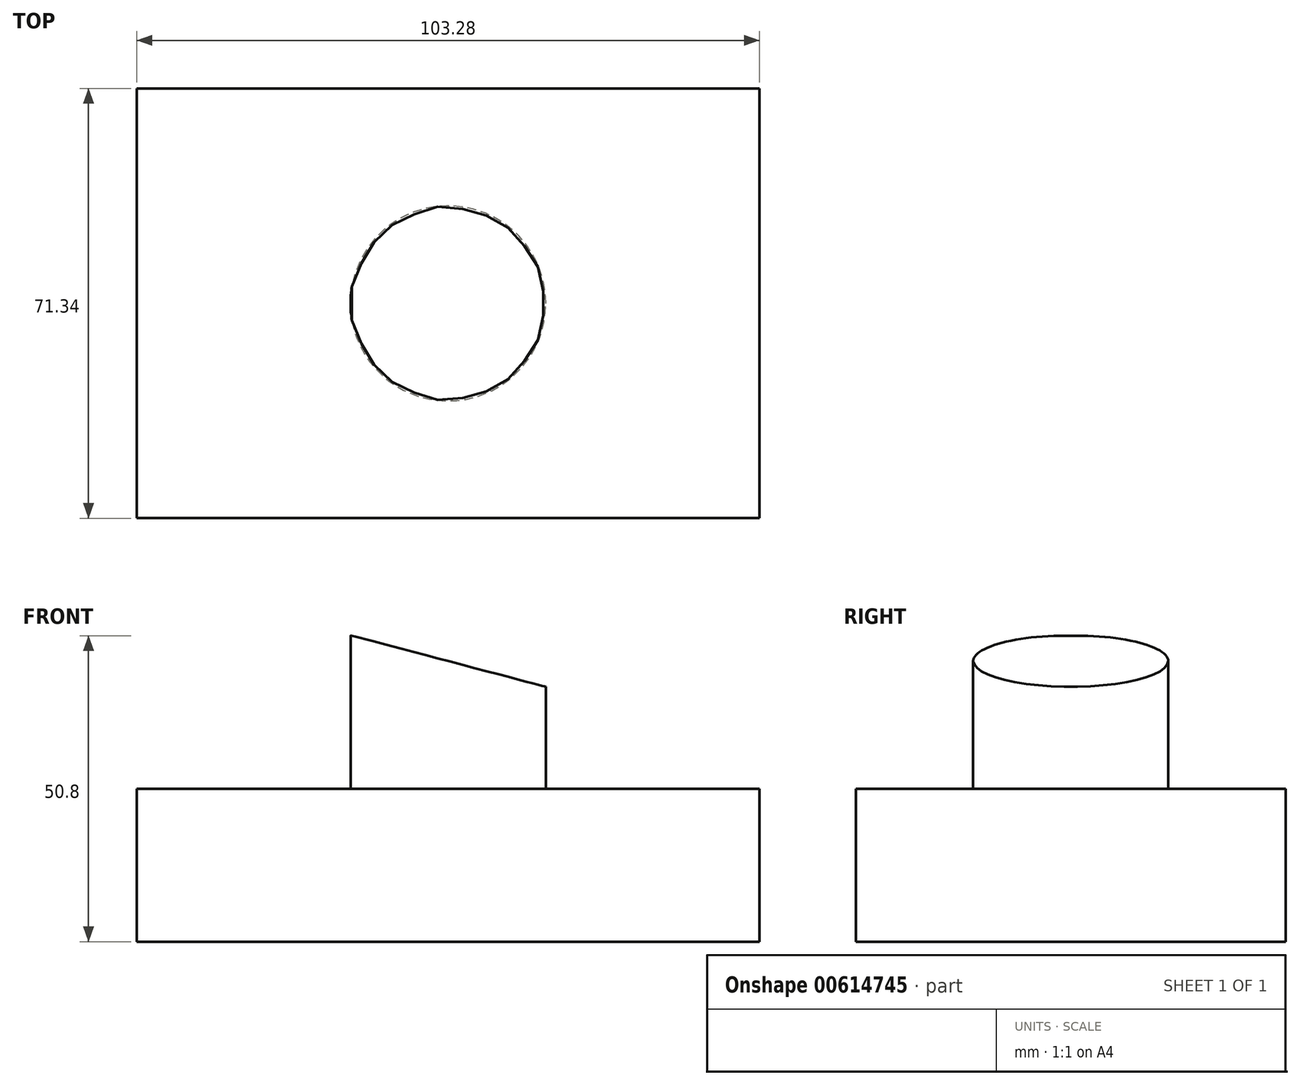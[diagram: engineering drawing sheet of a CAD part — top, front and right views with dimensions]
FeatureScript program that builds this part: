
annotation { "Feature Type Name" : "Feature", "Feature Type Description" : "" }
export const myFeature = defineFeature(function(context is Context, id is Id, definition is map)
    precondition{}
    {
        {
            var Q0;
            Q0=qCreatedBy(makeId("Top.planeOp"),FACE);
            var sketch = newSketch(context, id + "F0", { "sketchPlane" : qUnion([Q0])});
            skLineSegment(sketch, "E0.bottom", {"start": v(51.64, 35.67) * mm, "end": v(-51.64, 35.67) * mm});
            skLineSegment(sketch, "E0.top", {"start": v(51.64, -35.67) * mm, "end": v(-51.64, -35.67) * mm});
            skLineSegment(sketch, "E0.left", {"start": v(51.64, 35.67) * mm, "end": v(51.64, -35.67) * mm});
            skLineSegment(sketch, "E0.right", {"start": v(-51.64, 35.67) * mm, "end": v(-51.64, -35.67) * mm});
            skPoint(sketch, "E0.middle", {"position": v(0, 0) * mm});
            skSolve(sketch);
        }
        {
            var Q0;
            Q0=makeQuery(id+"F0.imprint","IMPRINT",FACE,{"disambiguationData":[TD([[makeQuery(id+"F0.imprint","IMPRINT",EDGE,{"derivedFrom":sQuery(id+"F0.wireOp",EDGE,"E0.bottom")}),1.0]])]});
            extrude(context, id + "F1", {"entities" : qUnion([Q0]), "depth" : 25.4 * mm, "offsetDistance" : 25.4 * mm});
        }
        {
            var Q0;
            Q0=makeQuery(id+"F1.opExtrude","CAP_FACE",FACE,{"disambiguationData":[OSD([sQuery(id+"F0.wireOp",EDGE,"E0.bottom"),sQuery(id+"F0.wireOp",EDGE,"E0.top"),sQuery(id+"F0.wireOp",EDGE,"E0.left"),sQuery(id+"F0.wireOp",EDGE,"E0.right")])],"isStart":false});
            var sketch = newSketch(context, id + "F2", { "sketchPlane" : qUnion([Q0])});
            skCircle(sketch, "E1", {"center": v(0, 0) * mm, "radius": 16.2 * mm});
            skSolve(sketch);
        }
        {
            var Q0;
            Q0=makeQuery(id+"F2.imprint","IMPRINT",FACE,{"disambiguationData":[TD([[makeQuery(id+"F2.imprint","IMPRINT",EDGE,{"derivedFrom":sQuery(id+"F2.wireOp",EDGE,"E1")}),1.0]])]});
            extrude(context, id + "F3", {"entities" : qUnion([Q0]), "operationType" : NewBodyOperationType.ADD, "depth" : 25.4 * mm, "offsetDistance" : 25.4 * mm});
        }
        {
            var Q0;
            Q0=qCreatedBy(makeId("Front.planeOp"),FACE);
            var sketch = newSketch(context, id + "F4", { "sketchPlane" : qUnion([Q0])});
            skLineSegment(sketch, "E2", {"start": v(-16.2, 50.87) * mm, "end": v(16.52, 50.87) * mm});
            skLineSegment(sketch, "E3", {"start": v(16.52, 50.87) * mm, "end": v(16.52, 42.23) * mm});
            skLineSegment(sketch, "E4", {"start": v(16.52, 42.23) * mm, "end": v(-16.2, 50.87) * mm});
            skSolve(sketch);
        }
        {
            var Q0;
            Q0 = qSketchRegion(id + "F4", true);
            extrude(context, id + "F5", {"entities" : qUnion([Q0]), "operationType" : NewBodyOperationType.REMOVE, "oppositeDirection" : true, "depth" : 25.4 * mm, "offsetDistance" : 25.4 * mm});
        }
        {
            var Q0;
            Q0=makeQuery(id+"F5.boolean.opBoolean","COPY",FACE,{"derivedFrom":makeQuery(id+"F5.opExtrude","CAP_FACE",FACE,{"disambiguationData":[OSD([sQuery(id+"F4.wireOp",EDGE,"E2"),sQuery(id+"F4.wireOp",EDGE,"E3"),sQuery(id+"F4.wireOp",EDGE,"E4")])],"isStart":true})});
            extrude(context, id + "F6", {"entities" : qUnion([Q0]), "operationType" : NewBodyOperationType.REMOVE, "oppositeDirection" : true, "depth" : 25.4 * mm, "offsetDistance" : 25.4 * mm});
        }
    });
